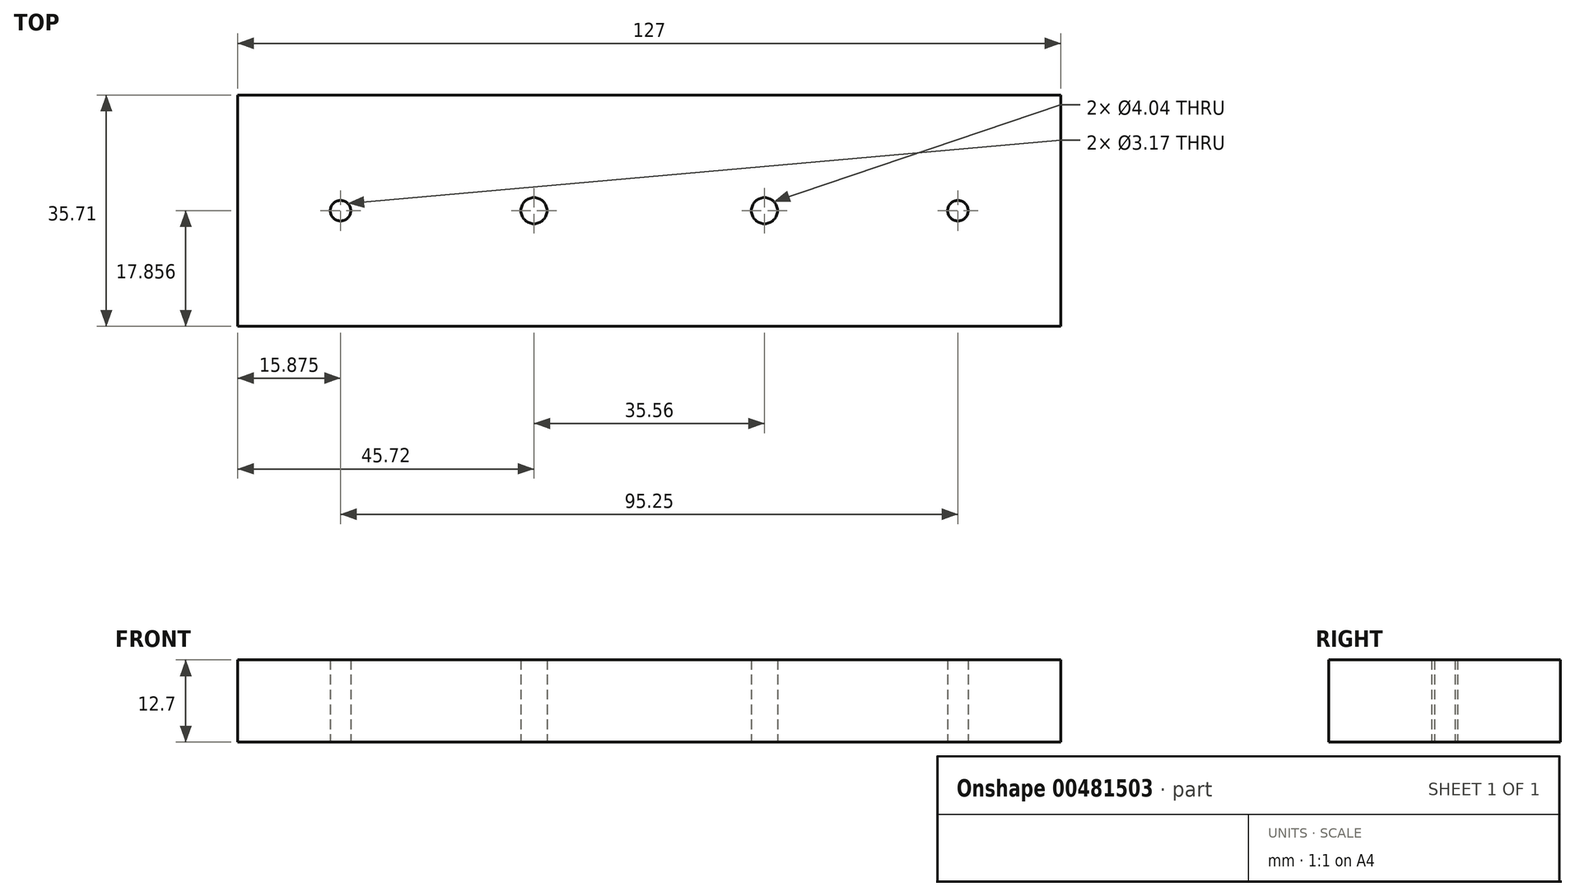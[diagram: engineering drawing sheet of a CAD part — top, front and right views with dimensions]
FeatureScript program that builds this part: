
annotation { "Feature Type Name" : "Feature", "Feature Type Description" : "" }
export const myFeature = defineFeature(function(context is Context, id is Id, definition is map)
    precondition{}
    {
        {
            var Q0;
            Q0=qCreatedBy(makeId("Top.planeOp"),FACE);
            var sketch = newSketch(context, id + "F0", { "sketchPlane" : qUnion([Q0])});
            skLineSegment(sketch, "E0.bottom", {"start": v(0, 0) * mm, "end": v(127, 0) * mm});
            skLineSegment(sketch, "E0.top", {"start": v(0, 35.71) * mm, "end": v(127, 35.71) * mm});
            skLineSegment(sketch, "E0.left", {"start": v(0, 0) * mm, "end": v(0, 35.71) * mm});
            skLineSegment(sketch, "E0.right", {"start": v(127, 0) * mm, "end": v(127, 35.71) * mm});
            skLineSegment(sketch, "E1", {"start": v(0, 35.71) * mm, "end": v(127, 0) * mm, "construction": true});
            skLineSegment(sketch, "E2", {"start": v(127, 35.71) * mm, "end": v(0, 0) * mm, "construction": true});
            skPoint(sketch, "E3", {"position": v(63.5, 17.86) * mm});
            skLineSegment(sketch, "E4", {"start": v(0, 17.86) * mm, "end": v(127, 17.86) * mm, "construction": true});
            skPoint(sketch, "E5", {"position": v(15.88, 17.86) * mm});
            skPoint(sketch, "E6", {"position": v(111.13, 17.86) * mm});
            skCircle(sketch, "E7", {"center": v(15.88, 17.86) * mm, "radius": 1.59 * mm});
            skCircle(sketch, "E8", {"center": v(111.13, 17.86) * mm, "radius": 1.59 * mm});
            skLineSegment(sketch, "E9.bottom", {"start": v(88.27, 12.3) * mm, "end": v(38.74, 12.3) * mm, "construction": true});
            skLineSegment(sketch, "E9.top", {"start": v(88.27, 23.4) * mm, "end": v(38.73, 23.4) * mm, "construction": true});
            skLineSegment(sketch, "E9.left", {"start": v(88.27, 12.3) * mm, "end": v(88.27, 23.4) * mm, "construction": true});
            skLineSegment(sketch, "E9.right", {"start": v(38.74, 12.3) * mm, "end": v(38.74, 23.4) * mm, "construction": true});
            skCircle(sketch, "E10", {"center": v(45.72, 17.86) * mm, "radius": 2.02 * mm});
            skCircle(sketch, "E11", {"center": v(81.28, 17.86) * mm, "radius": 2.02 * mm});
            skCircle(sketch, "E12", {"center": v(45.72, 17.86) * mm, "radius": 4.62 * mm});
            skCircle(sketch, "E13", {"center": v(81.28, 17.86) * mm, "radius": 4.62 * mm});
            skSolve(sketch);
        }
        {
            var Q0;
            Q0=makeQuery(id+"F0.imprint","IMPRINT",FACE,{"disambiguationData":[TD([[makeQuery(id+"F0.imprint","IMPRINT",EDGE,{"derivedFrom":sQuery(id+"F0.wireOp",EDGE,"E0.bottom")}),1.0]])]});
            var Q1;
            Q1=makeQuery(id+"F0.imprint","IMPRINT",FACE,{"disambiguationData":[TD([[makeQuery(id+"F0.imprint","IMPRINT",EDGE,{"derivedFrom":sQuery(id+"F0.wireOp",EDGE,"E10")}),-1.0]])]});
            var Q2;
            Q2=makeQuery(id+"F0.imprint","IMPRINT",FACE,{"disambiguationData":[TD([[makeQuery(id+"F0.imprint","IMPRINT",EDGE,{"derivedFrom":sQuery(id+"F0.wireOp",EDGE,"E11")}),-1.0]])]});
            extrude(context, id + "F1", {"entities" : qUnion([Q0, Q1, Q2]), "depth" : 12.7 * mm, "offsetDistance" : 25.4 * mm});
        }
        {
            var Q0;
            Q0=makeQuery(id+"F1.opExtrude","SWEPT_FACE",FACE,{"disambiguationData":[OSD([sQuery(id+"F0.wireOp",EDGE,"E0.top")])]});
            cPlane(context, id + "F2", {"entities" : qUnion([Q0]), "cplaneType" : CPlaneType.OFFSET, "offset" : 3.17 * mm, "width" : 152.4 * mm, "height" : 152.4 * mm});
        }
    });
